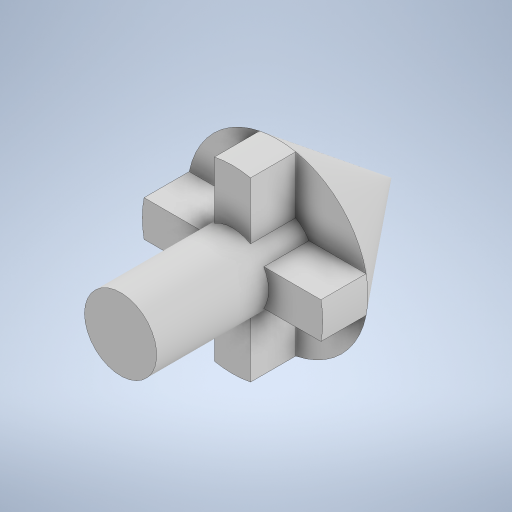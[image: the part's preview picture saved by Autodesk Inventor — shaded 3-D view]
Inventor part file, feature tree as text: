
AUTODESK INVENTOR PART (.ipt)
format: ipt  version: 2023 (Build 270158000, 158)  size: 280,576 bytes
history: native  units: mm
features: sketch x2, revolve x1, extrude x1
ambient origin geometry x8: Origin, YZ Plane, XZ Plane, XY Plane, X Axis, Y Axis, Z Axis, Center Point
bodies: Solid1 (feature_tree)
feature tree (4):
  revolve  "Revolution1"  [1 undecoded]
  extrude  "Extrusion1"  Depth=8.7mm
  sketch  "Sketch1"  dims[d0=15.0mm d1=5.0mm]
  sketch  "Sketch2"  dims[d3=2.0mm d5=8.7mm d7=90.0deg d8=1.0mm d9=40.0mm d11=360.0deg d13=2.5mm d14=0.0mm]
note: 1 required parameter value undecoded (feature->parameter linkage not recoverable at this tier; creation-order binding heuristic only, values carry confidence <= 0.55)
